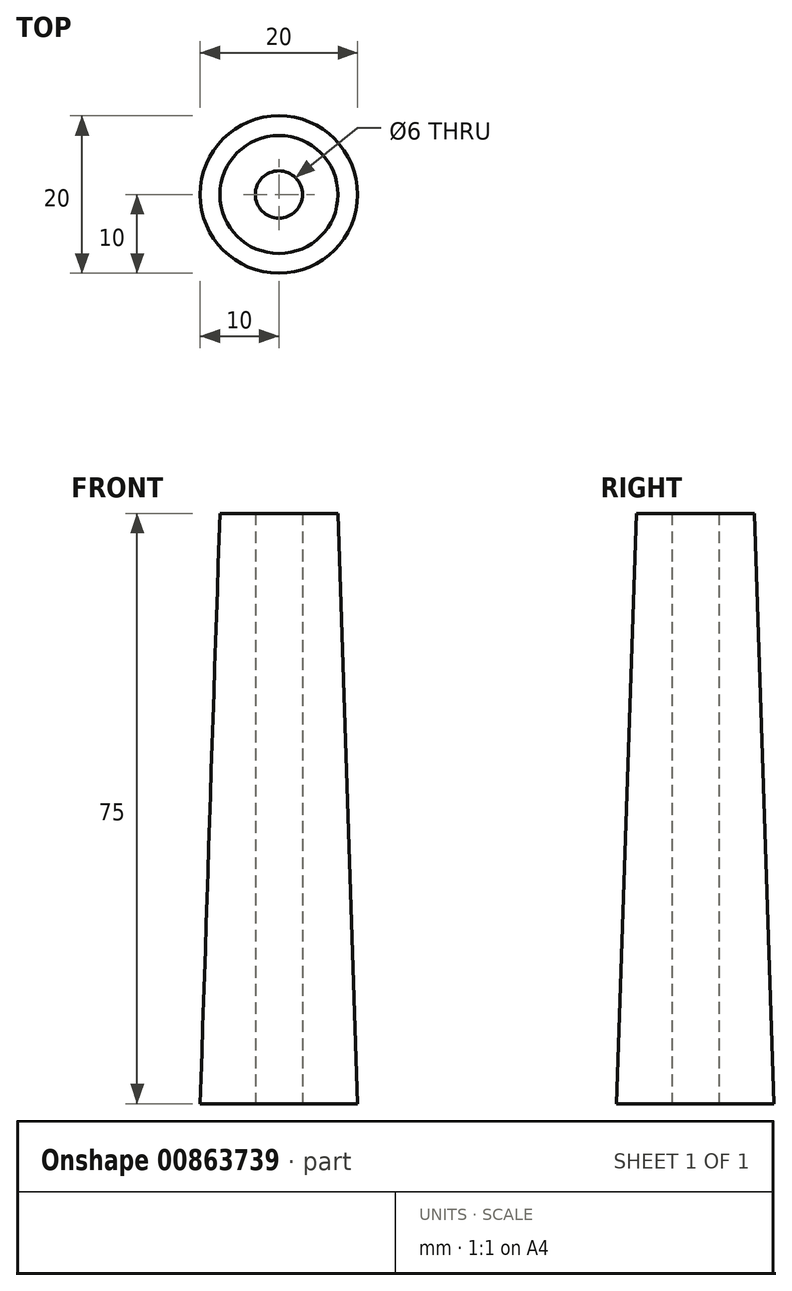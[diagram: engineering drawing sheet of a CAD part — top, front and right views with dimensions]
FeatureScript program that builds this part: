
annotation { "Feature Type Name" : "Feature", "Feature Type Description" : "" }
export const myFeature = defineFeature(function(context is Context, id is Id, definition is map)
    precondition{}
    {
        {
            var Q0;
            Q0=qCreatedBy(makeId("Front.planeOp"),FACE);
            var sketch = newSketch(context, id + "F0", { "sketchPlane" : qUnion([Q0])});
            skLineSegment(sketch, "E0", {"start": v(0, 0) * mm, "end": v(0, 75) * mm, "construction": true});
            skLineSegment(sketch, "E1", {"start": v(-3, 75) * mm, "end": v(-7.5, 75) * mm});
            skLineSegment(sketch, "E2", {"start": v(-7.5, 75) * mm, "end": v(-10, 0) * mm});
            skLineSegment(sketch, "E3", {"start": v(-10, 0) * mm, "end": v(-3, 0) * mm});
            skLineSegment(sketch, "E4", {"start": v(-3, 0) * mm, "end": v(-3, 75) * mm});
            skSolve(sketch);
        }
        {
            var Q0;
            Q0=makeQuery(id+"F0.imprint","IMPRINT",FACE,{"disambiguationData":[TD([[makeQuery(id+"F0.imprint","IMPRINT",EDGE,{"derivedFrom":sQuery(id+"F0.wireOp",EDGE,"E1")}),1.0]])]});
            var Q1;
            Q1=sQuery(id+"F0.wireOp",EDGE,"E0");
            revolve(context, id + "F1", {"surfaceOperationType" : NewSurfaceOperationType.NEW, "entities" : qUnion([Q0]), "axis" : qUnion([Q1]), "revolveType" : RevolveType.FULL});
        }
    });
